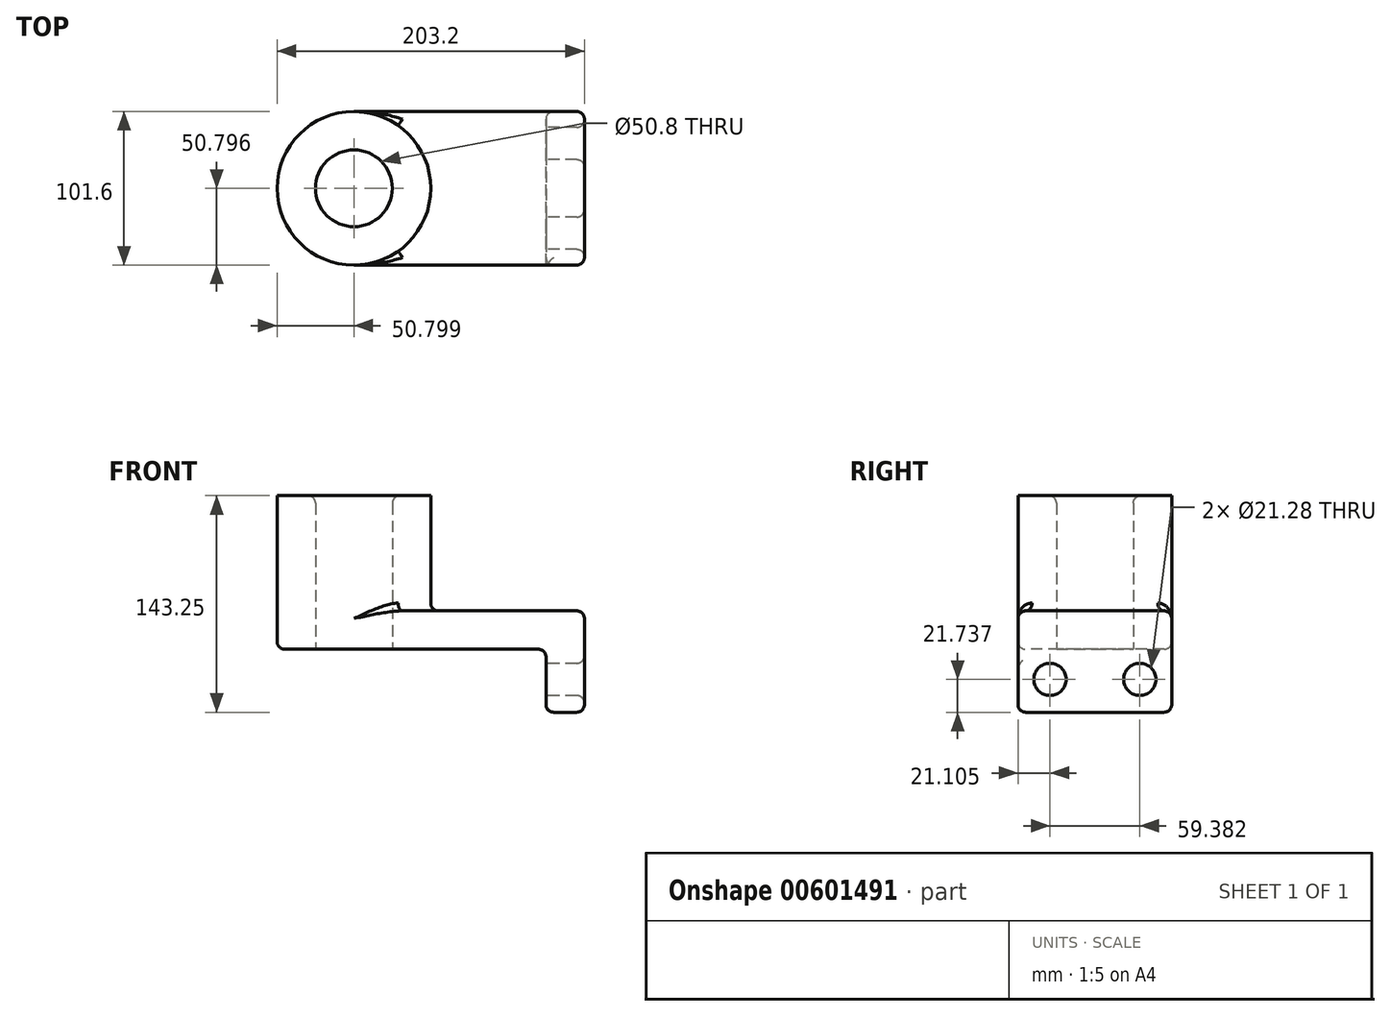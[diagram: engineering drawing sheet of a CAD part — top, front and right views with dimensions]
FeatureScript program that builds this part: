
annotation { "Feature Type Name" : "Feature", "Feature Type Description" : "" }
export const myFeature = defineFeature(function(context is Context, id is Id, definition is map)
    precondition{}
    {
        {
            var Q0;
            Q0=qCreatedBy(makeId("Top.planeOp"),FACE);
            var sketch = newSketch(context, id + "F0", { "sketchPlane" : qUnion([Q0])});
            skLineSegment(sketch, "E0.bottom", {"start": v(-47.18, 54.93) * mm, "end": v(79.82, 54.93) * mm});
            skLineSegment(sketch, "E0.top", {"start": v(-47.18, -46.67) * mm, "end": v(79.82, -46.67) * mm});
            skLineSegment(sketch, "E0.left", {"start": v(-47.18, 54.93) * mm, "end": v(-47.18, -46.67) * mm});
            skLineSegment(sketch, "E0.right", {"start": v(79.82, 54.93) * mm, "end": v(79.82, -46.67) * mm});
            skCircle(sketch, "E1", {"center": v(-47.18, 4.13) * mm, "radius": 50.8 * mm});
            skCircle(sketch, "E2", {"center": v(-47.18, 4.13) * mm, "radius": 25.4 * mm});
            skSolve(sketch);
        }
        {
            var Q0;
            Q0 = qSketchRegion(id + "F0", true);
            extrude(context, id + "F1", {"entities" : qUnion([Q0]), "depth" : 25.4 * mm, "offsetDistance" : 25.4 * mm});
        }
        {
            var Q0;
            Q0=makeQuery(id+"F1.opExtrude","SWEPT_FACE",FACE,{"disambiguationData":[OSD([sQuery(id+"F0.wireOp",EDGE,"E0.right")])]});
            var sketch = newSketch(context, id + "F2", { "sketchPlane" : qUnion([Q0])});
            skLineSegment(sketch, "E3.bottom", {"start": v(-46.67, 25.4) * mm, "end": v(54.93, 25.4) * mm});
            skLineSegment(sketch, "E3.top", {"start": v(-46.67, -41.65) * mm, "end": v(54.93, -41.65) * mm});
            skLineSegment(sketch, "E3.left", {"start": v(-46.67, 25.4) * mm, "end": v(-46.67, -41.65) * mm});
            skLineSegment(sketch, "E3.right", {"start": v(54.93, 25.4) * mm, "end": v(54.93, -41.65) * mm});
            skCircle(sketch, "E4", {"center": v(-25.57, -19.91) * mm, "radius": 10.64 * mm});
            skLineSegment(sketch, "E5", {"start": v(4.13, 25.4) * mm, "end": v(4.13, -41.65) * mm, "construction": true});
            skCircle(sketch, "E6.MirrorC", {"center": v(33.82, -19.91) * mm, "radius": 10.64 * mm});
            skSolve(sketch);
        }
        {
            var Q0;
            Q0 = qSketchRegion(id + "F2", true);
            extrude(context, id + "F3", {"entities" : qUnion([Q0]), "operationType" : NewBodyOperationType.ADD, "depth" : 25.4 * mm, "offsetDistance" : 25.4 * mm});
        }
        {
            var Q0;
            {var subQ1=sQuery(id+"F0.wireOp",EDGE,"E0.left");var subQ3=sQuery(id+"F0.wireOp",EDGE,"E2");var subQ4=makeQuery(id+"F0.imprint","INTERSECT",VERTEX,{"disambiguationData":[OD(0.0)],"derivedFrom":[subQ1,subQ3]});Q0=makeQuery(id+"F0.imprint","IMPRINT",FACE,{"disambiguationData":[TD([[makeQuery(id+"F0.imprint","IMPRINT",EDGE,{"disambiguationData":[TD([[subQ4,1.0]])],"derivedFrom":subQ3}),-1.0]])]});}
            var Q1;
            {var subQ1=sQuery(id+"F0.wireOp",EDGE,"E0.left");var subQ3=sQuery(id+"F0.wireOp",EDGE,"E2");var subQ4=makeQuery(id+"F0.imprint","INTERSECT",VERTEX,{"disambiguationData":[OD(0.0)],"derivedFrom":[subQ1,subQ3]});Q1=makeQuery(id+"F0.imprint","IMPRINT",FACE,{"disambiguationData":[TD([[makeQuery(id+"F0.imprint","IMPRINT",EDGE,{"disambiguationData":[TD([[subQ4,-1.0]])],"derivedFrom":subQ3}),-1.0]])]});}
            extrude(context, id + "F4", {"entities" : qUnion([Q0, Q1]), "operationType" : NewBodyOperationType.ADD, "depth" : 101.6 * mm, "offsetDistance" : 25.4 * mm});
        }
        {
            var Q0;
            Q0=makeQuery(id+"F4.opExtrude","CAP_EDGE",EDGE,{"disambiguationData":[OSD([sQuery(id+"F0.wireOp",EDGE,"E2")])],"isStart":false});
            var Q1;
            Q1=makeQuery(id+"F3.boolean.opBoolean","MERGE",FACE,{"derivedFrom":[makeQuery(id+"F1.opExtrude","CAP_FACE",FACE,{"disambiguationData":[OSD([sQuery(id+"F0.wireOp",EDGE,"E0.bottom"),sQuery(id+"F0.wireOp",EDGE,"E0.top"),sQuery(id+"F0.wireOp",EDGE,"E0.right"),sQuery(id+"F0.wireOp",EDGE,"E1"),sQuery(id+"F0.wireOp",EDGE,"E2")])],"isStart":false}),makeQuery(id+"F3.opExtrude","SWEPT_FACE",FACE,{"disambiguationData":[OSD([sQuery(id+"F2.wireOp",EDGE,"E3.bottom")])]})]});
            var Q2;
            Q2=makeQuery(id+"F1.opExtrude","CAP_EDGE",EDGE,{"disambiguationData":[OSD([sQuery(id+"F0.wireOp",EDGE,"E0.top")])],"isStart":true});
            var Q3;
            Q3=makeQuery(id+"F3.opExtrude","CAP_EDGE",EDGE,{"disambiguationData":[OSD([sQuery(id+"F2.wireOp",EDGE,"E3.right")])],"isStart":false});
            var Q4;
            Q4=makeQuery(id+"F3.opExtrude","CAP_FACE",FACE,{"disambiguationData":[OSD([sQuery(id+"F2.wireOp",EDGE,"E3.bottom"),sQuery(id+"F2.wireOp",EDGE,"E3.top"),sQuery(id+"F2.wireOp",EDGE,"E3.left"),sQuery(id+"F2.wireOp",EDGE,"E3.right"),sQuery(id+"F2.wireOp",EDGE,"E4"),sQuery(id+"F2.wireOp",EDGE,"E6.MirrorC")])],"isStart":false});
            var Q5;
            Q5=makeQuery(id+"F3.opExtrude","CAP_EDGE",EDGE,{"disambiguationData":[OSD([sQuery(id+"F2.wireOp",EDGE,"E3.right")])],"isStart":true});
            var Q6;
            Q6=makeQuery(id+"F3.opExtrude","SWEPT_FACE",FACE,{"disambiguationData":[OSD([sQuery(id+"F2.wireOp",EDGE,"E3.top")])]});
            var Q7;
            Q7=makeQuery(id+"F1.opExtrude","CAP_EDGE",EDGE,{"disambiguationData":[OSD([sQuery(id+"F0.wireOp",EDGE,"E0.right")])],"isStart":true});
            fillet(context, id + "F5", {"entities" : qUnion([Q0, Q1, Q2, Q3, Q4, Q5, Q6, Q7]), "radius" : 5.08 * mm, "tangentPropagation" : true, "allowEdgeOverflow" : false});
        }
    });
